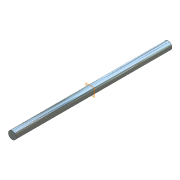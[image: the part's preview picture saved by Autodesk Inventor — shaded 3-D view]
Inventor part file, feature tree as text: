
AUTODESK INVENTOR PART (.ipt)
format: ipt  version: unknown  size: 158,208 bytes
history: native  units: mm (DEFAULTED — no unit token found)
features: extrude x1, plane x1, sketch x1
ambient origin geometry x8: Origin, YZ Plane, XZ Plane, XY Plane, X Axis, Y Axis, Z Axis, Center Point
feature tree (3):
  extrude  "Extrusion1"  Depth=254.0mm TaperAngle=0.0deg
  plane  "Work Plane1"
  sketch  "Sketch1"  dims[d0=12.7mm d1=254.0mm d2=0.0mm]
